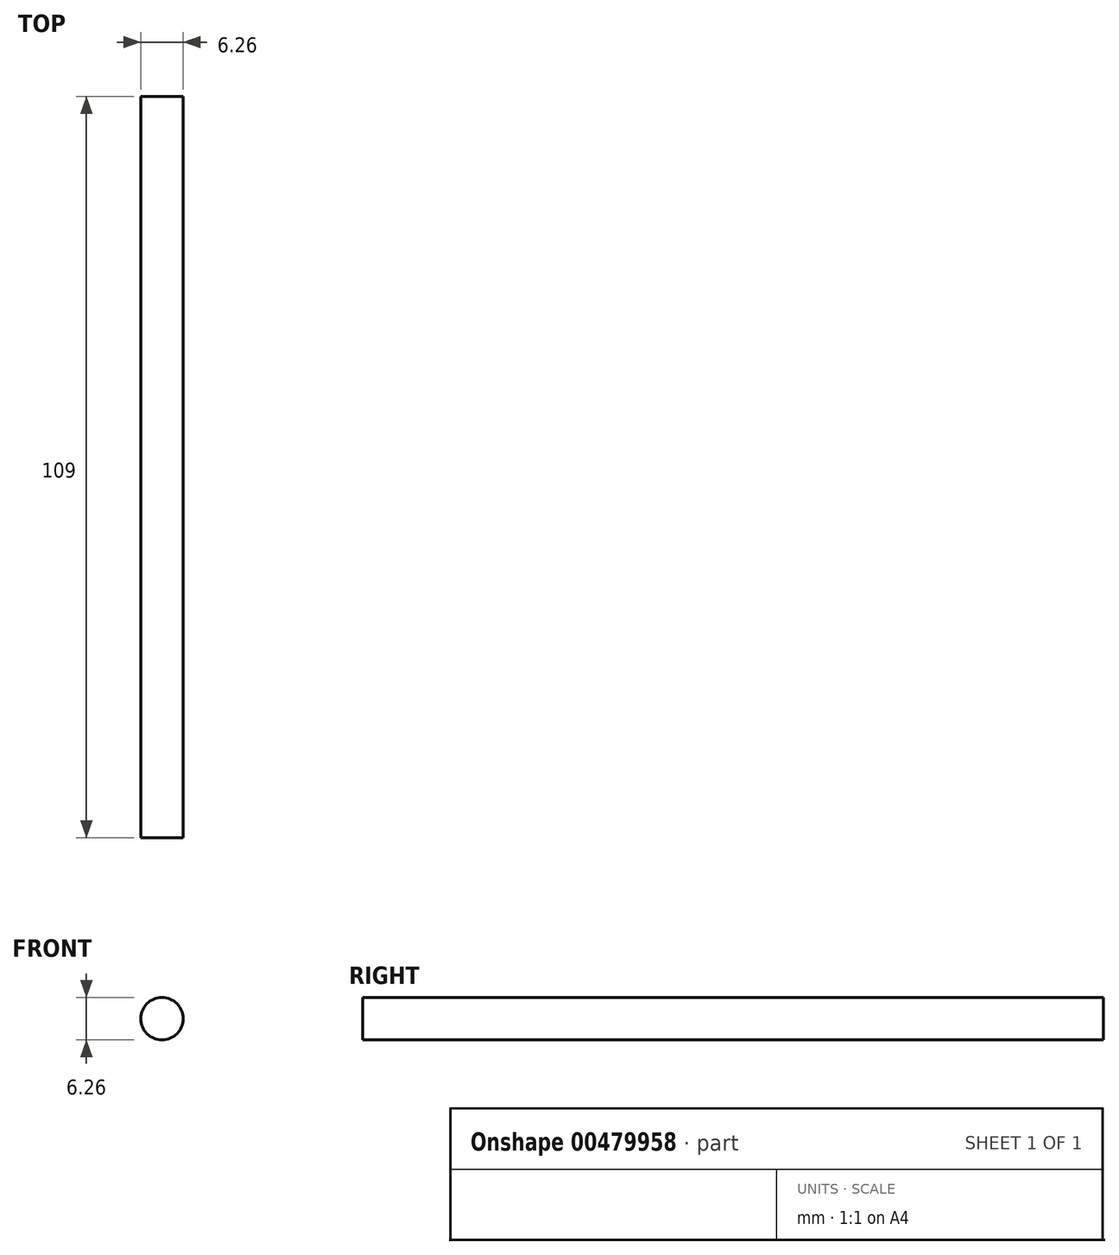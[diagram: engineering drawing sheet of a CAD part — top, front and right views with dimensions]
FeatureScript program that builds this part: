
annotation { "Feature Type Name" : "Feature", "Feature Type Description" : "" }
export const myFeature = defineFeature(function(context is Context, id is Id, definition is map)
    precondition{}
    {
        {
            var Q0;
            Q0=qCreatedBy(makeId("Front.planeOp"),FACE);
            var sketch = newSketch(context, id + "F0", { "sketchPlane" : qUnion([Q0])});
            skCircle(sketch, "E0", {"center": v(0, 0) * mm, "radius": 3.13 * mm});
            skSolve(sketch);
        }
        {
            var Q0;
            Q0=makeQuery(id+"F0.imprint","IMPRINT",FACE,{"disambiguationData":[TD([[makeQuery(id+"F0.imprint","IMPRINT",EDGE,{"derivedFrom":sQuery(id+"F0.wireOp",EDGE,"E0")}),1.0]])]});
            extrude(context, id + "F1", {"entities" : qUnion([Q0]), "depth" : 109 * mm});
        }
    });
